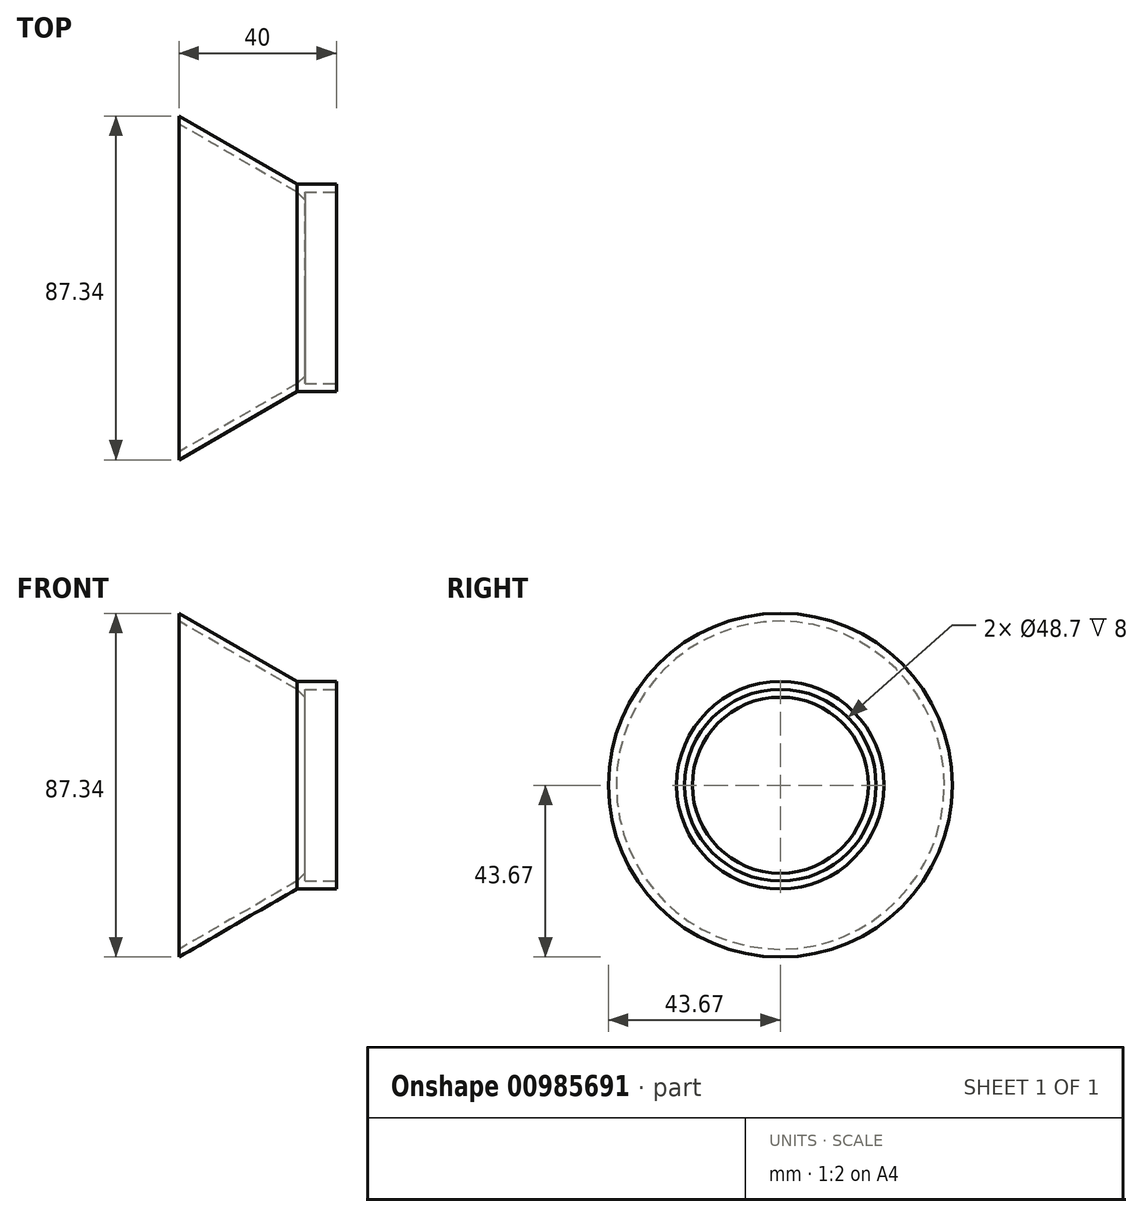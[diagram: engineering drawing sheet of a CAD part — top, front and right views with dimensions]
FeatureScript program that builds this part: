
annotation { "Feature Type Name" : "Feature", "Feature Type Description" : "" }
export const myFeature = defineFeature(function(context is Context, id is Id, definition is map)
    precondition{}
    {
        {
            var Q0;
            Q0=qCreatedBy(makeId("Front.planeOp"),FACE);
            var sketch = newSketch(context, id + "F0", { "sketchPlane" : qUnion([Q0])});
            skLineSegment(sketch, "E0", {"start": v(0, 0) * mm, "end": v(-30, 0) * mm, "construction": true});
            skLineSegment(sketch, "E1", {"start": v(-30, 0) * mm, "end": v(-30, -43.67) * mm, "construction": true});
            skLineSegment(sketch, "E2", {"start": v(-30, -43.67) * mm, "end": v(0, -26.35) * mm});
            skLineSegment(sketch, "E3", {"start": v(0, -26.35) * mm, "end": v(10, -26.35) * mm});
            skLineSegment(sketch, "E4", {"start": v(10, -26.35) * mm, "end": v(10, 0) * mm, "construction": true});
            skLineSegment(sketch, "E5", {"start": v(10, 0) * mm, "end": v(0, 0) * mm, "construction": true});
            skLineSegment(sketch, "E6", {"start": v(5, -26.35) * mm, "end": v(5, 0) * mm, "construction": true});
            skLineSegment(sketch, "E7", {"start": v(10, -24.35) * mm, "end": v(2, -24.35) * mm});
            skLineSegment(sketch, "E8", {"start": v(2, -24.35) * mm, "end": v(2, -22.35) * mm});
            skLineSegment(sketch, "E9", {"start": v(0, -24.35) * mm, "end": v(0, -24.35) * mm});
            skLineSegment(sketch, "E10", {"start": v(2, -22.35) * mm, "end": v(0, -24.35) * mm});
            skLineSegment(sketch, "E11", {"start": v(0, -24.35) * mm, "end": v(-30, -41.67) * mm});
            skLineSegment(sketch, "E12", {"start": v(-30, -41.67) * mm, "end": v(-30, -43.67) * mm});
            skLineSegment(sketch, "E13", {"start": v(10, -24.35) * mm, "end": v(10, -26.35) * mm});
            skSolve(sketch);
        }
        {
            var Q0;
            Q0 = qSketchRegion(id + "F0", true);
            var Q1;
            Q1=sQuery(id+"F0.wireOp",EDGE,"E0");
            revolve(context, id + "F1", {"surfaceOperationType" : NewSurfaceOperationType.NEW, "entities" : qUnion([Q0]), "axis" : qUnion([Q1]), "revolveType" : RevolveType.FULL});
        }
        {
            var Q0;
            Q0 = qSketchRegion(id + "F0", true);
            var Q1;
            Q1=sQuery(id+"F0.wireOp",EDGE,"E0");
            revolve(context, id + "F2", {"surfaceOperationType" : NewSurfaceOperationType.NEW, "entities" : qUnion([Q0]), "axis" : qUnion([Q1]), "revolveType" : RevolveType.FULL});
        }
    });
